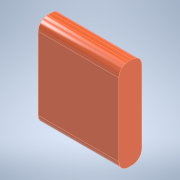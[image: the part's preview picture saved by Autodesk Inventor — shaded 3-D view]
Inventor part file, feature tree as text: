
AUTODESK INVENTOR PART (.ipt)
format: ipt  version: 2022 (Build 260153000, 153)  size: 105,472 bytes
history: native  units: mm
features: other x1, extrude x1, fillet x1, sketch x1
ambient origin geometry x8: Origin, YZ Plane, XZ Plane, XY Plane, X Axis, Y Axis, Z Axis, Center Point
bodies: Body1 (feature_tree)
feature tree (4):
  other  "ソリッド1"
  extrude  "押し出し1"  Depth=51.0mm
  fillet  "フィレット1"  Radius=58.0mm
  sketch  "スケッチ1"
